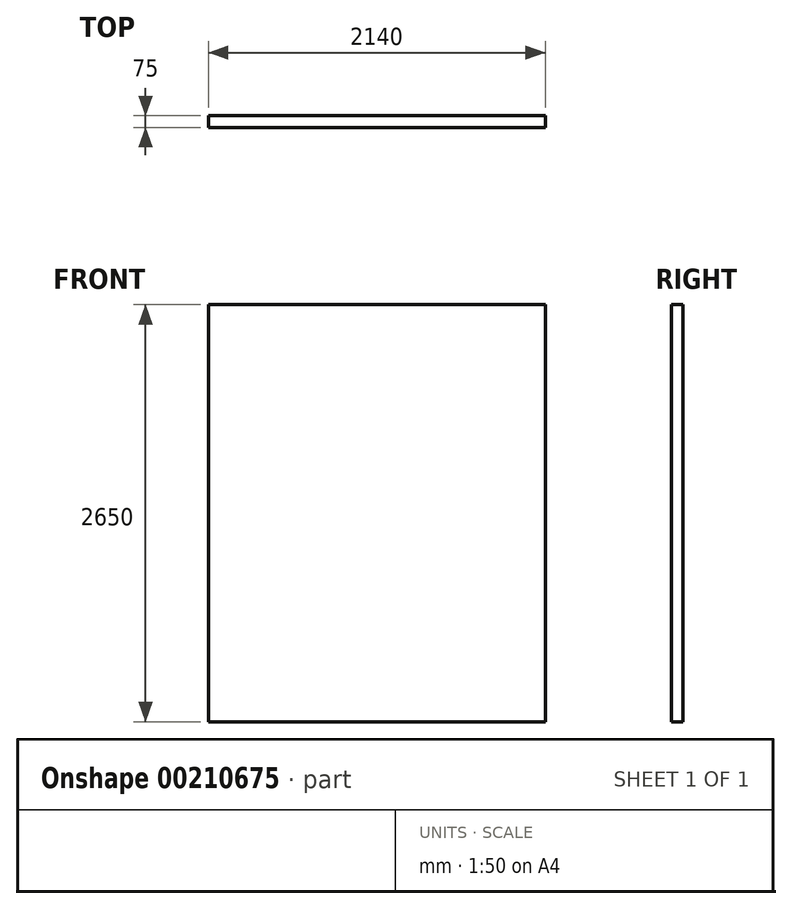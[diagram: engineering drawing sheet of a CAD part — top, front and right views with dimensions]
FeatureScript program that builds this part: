
annotation { "Feature Type Name" : "Feature", "Feature Type Description" : "" }
export const myFeature = defineFeature(function(context is Context, id is Id, definition is map)
    precondition{}
    {
        {
            var Q0;
            Q0=qCreatedBy(makeId("Front.planeOp"),FACE);
            var sketch = newSketch(context, id + "F0", { "sketchPlane" : qUnion([Q0])});
            skLineSegment(sketch, "E0.bottom", {"start": v(0, 0) * mm, "end": v(2140, 0) * mm});
            skLineSegment(sketch, "E0.top", {"start": v(0, 2650) * mm, "end": v(2140, 2650) * mm});
            skLineSegment(sketch, "E0.left", {"start": v(0, 0) * mm, "end": v(0, 2650) * mm});
            skLineSegment(sketch, "E0.right", {"start": v(2140, 0) * mm, "end": v(2140, 2650) * mm});
            skSolve(sketch);
        }
        {
            var Q0;
            Q0=makeQuery(id+"F0.imprint","IMPRINT",FACE,{"disambiguationData":[TD([[makeQuery(id+"F0.imprint","IMPRINT",EDGE,{"derivedFrom":sQuery(id+"F0.wireOp",EDGE,"E0.bottom")}),1.0]])]});
            extrude(context, id + "F1", {"entities" : qUnion([Q0]), "depth" : 75 * mm});
        }
    });
